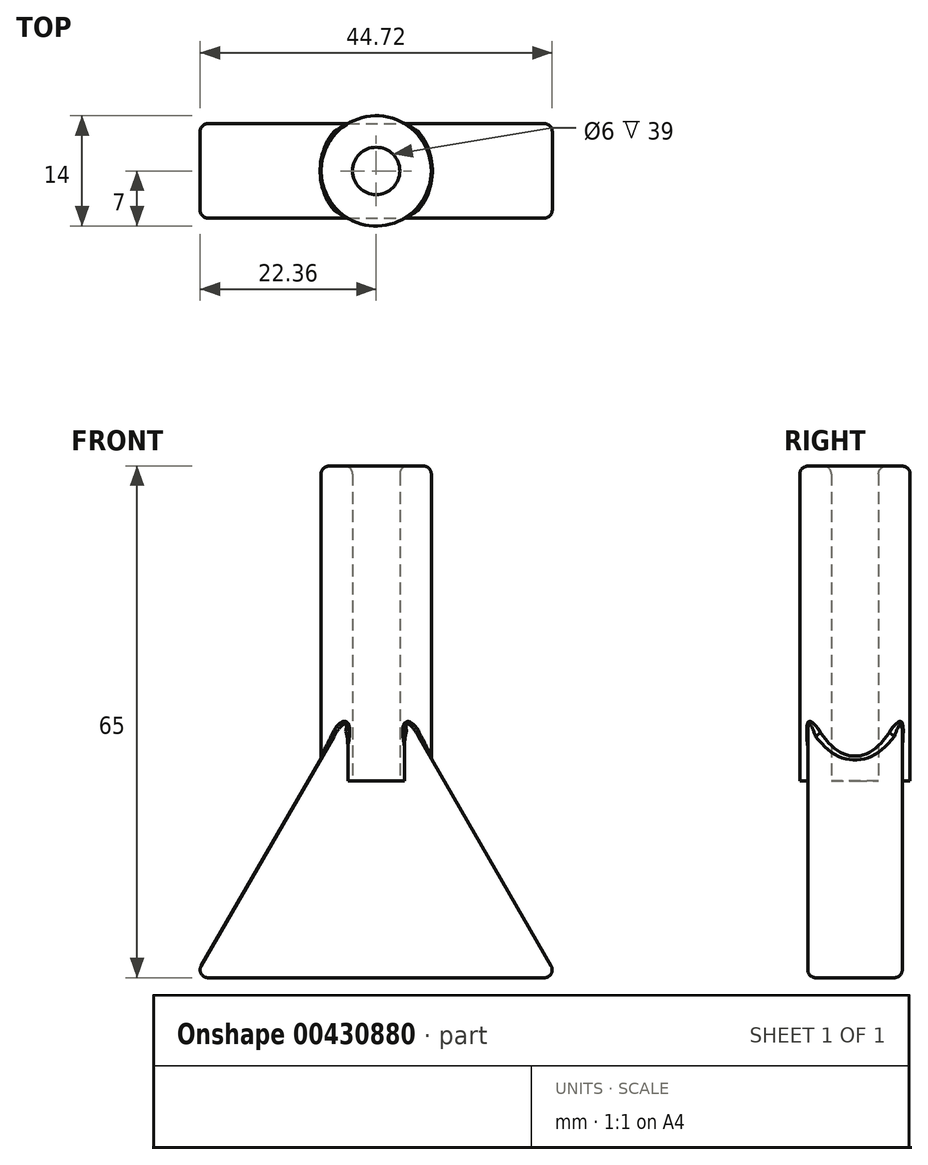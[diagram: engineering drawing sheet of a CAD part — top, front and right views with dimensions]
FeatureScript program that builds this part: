
annotation { "Feature Type Name" : "Feature", "Feature Type Description" : "" }
export const myFeature = defineFeature(function(context is Context, id is Id, definition is map)
    precondition{}
    {
        {
            var Q0;
            Q0=qCreatedBy(makeId("Top.planeOp"),FACE);
            var sketch = newSketch(context, id + "F0", { "sketchPlane" : qUnion([Q0])});
            skCircle(sketch, "E0", {"center": v(0, 0) * mm, "radius": 3 * mm});
            skCircle(sketch, "E1", {"center": v(0, 0) * mm, "radius": 7 * mm});
            skSolve(sketch);
        }
        {
            var Q0;
            Q0=makeQuery(id+"F0.imprint","IMPRINT",FACE,{"disambiguationData":[TD([[makeQuery(id+"F0.imprint","IMPRINT",EDGE,{"derivedFrom":sQuery(id+"F0.wireOp",EDGE,"E0")}),-1.0]])]});
            extrude(context, id + "F1", {"entities" : qUnion([Q0]), "depth" : 40 * mm});
        }
        {
            var Q0;
            Q0=qCreatedBy(makeId("Front.planeOp"),FACE);
            var sketch = newSketch(context, id + "F2", { "sketchPlane" : qUnion([Q0])});
            skLineSegment(sketch, "E2", {"start": v(0, 15) * mm, "end": v(-23.1, -25) * mm});
            skLineSegment(sketch, "E3", {"start": v(-23.1, -25) * mm, "end": v(23.1, -25) * mm});
            skLineSegment(sketch, "E4", {"start": v(23.1, -25) * mm, "end": v(0, 15) * mm});
            skSolve(sketch);
        }
        {
            var Q0;
            Q0=makeQuery(id+"F2.imprint","IMPRINT",FACE,{"disambiguationData":[TD([[makeQuery(id+"F2.imprint","IMPRINT",EDGE,{"derivedFrom":sQuery(id+"F2.wireOp",EDGE,"E2")}),1.0]])]});
            extrude(context, id + "F3", {"entities" : qUnion([Q0]), "operationType" : NewBodyOperationType.ADD, "endBound" : BoundingType.SYMMETRIC, "depth" : 12 * mm});
        }
        {
            var Q0;
            Q0=makeQuery(id+"F3.opExtrude","CAP_EDGE",EDGE,{"disambiguationData":[OSD([sQuery(id+"F2.wireOp",EDGE,"E2")])],"isStart":false});
            var Q1;
            Q1=makeQuery(id+"F3.opExtrude","CAP_EDGE",EDGE,{"disambiguationData":[OSD([sQuery(id+"F2.wireOp",EDGE,"E2")])],"isStart":true});
            var Q2;
            Q2=makeQuery(id+"F3.opExtrude","CAP_EDGE",EDGE,{"disambiguationData":[OSD([sQuery(id+"F2.wireOp",EDGE,"E4")])],"isStart":false});
            var Q3;
            Q3=makeQuery(id+"F3.opExtrude","CAP_EDGE",EDGE,{"disambiguationData":[OSD([sQuery(id+"F2.wireOp",EDGE,"E4")])],"isStart":true});
            var Q4;
            Q4=makeQuery(id+"F3.boolean.opBoolean","INTERSECT",EDGE,{"derivedFrom":[makeQuery(id+"F1.opExtrude","SWEPT_FACE",FACE,{"disambiguationData":[OSD([sQuery(id+"F0.wireOp",EDGE,"E1")])]}),makeQuery(id+"F3.opExtrude","SWEPT_FACE",FACE,{"disambiguationData":[OSD([sQuery(id+"F2.wireOp",EDGE,"E4")])]})]});
            var Q5;
            Q5=makeQuery(id+"F3.boolean.opBoolean","INTERSECT",EDGE,{"derivedFrom":[makeQuery(id+"F1.opExtrude","SWEPT_FACE",FACE,{"disambiguationData":[OSD([sQuery(id+"F0.wireOp",EDGE,"E1")])]}),makeQuery(id+"F3.opExtrude","SWEPT_FACE",FACE,{"disambiguationData":[OSD([sQuery(id+"F2.wireOp",EDGE,"E2")])]})]});
            var Q6;
            Q6=makeQuery(id+"F3.opExtrude","SWEPT_EDGE",EDGE,{"disambiguationData":[OSD([sQuery(id+"F2.wireOp",EDGE,"E2"),sQuery(id+"F2.wireOp",EDGE,"E3")])]});
            var Q7;
            Q7=makeQuery(id+"F3.opExtrude","CAP_EDGE",EDGE,{"disambiguationData":[OSD([sQuery(id+"F2.wireOp",EDGE,"E3")])],"isStart":false});
            var Q8;
            Q8=makeQuery(id+"F3.opExtrude","CAP_EDGE",EDGE,{"disambiguationData":[OSD([sQuery(id+"F2.wireOp",EDGE,"E3")])],"isStart":true});
            var Q9;
            Q9=makeQuery(id+"F3.opExtrude","SWEPT_EDGE",EDGE,{"disambiguationData":[OSD([sQuery(id+"F2.wireOp",EDGE,"E3"),sQuery(id+"F2.wireOp",EDGE,"E4")])]});
            fillet(context, id + "F4", {"entities" : qUnion([Q0, Q1, Q2, Q3, Q4, Q5, Q6, Q7, Q8, Q9]), "radius" : 1 * mm, "tangentPropagation" : true, "allowEdgeOverflow" : false});
        }
        {
            var Q0;
            Q0=makeQuery(id+"F1.opExtrude","CAP_EDGE",EDGE,{"disambiguationData":[OSD([sQuery(id+"F0.wireOp",EDGE,"E0")])],"isStart":false});
            var Q1;
            Q1=makeQuery(id+"F1.opExtrude","CAP_EDGE",EDGE,{"disambiguationData":[OSD([sQuery(id+"F0.wireOp",EDGE,"E1")])],"isStart":false});
            fillet(context, id + "F5", {"entities" : qUnion([Q0, Q1]), "radius" : 1 * mm, "tangentPropagation" : true, "allowEdgeOverflow" : false});
        }
        {
            var Q0;
            Q0=qCreatedBy(makeId("Top.planeOp"),FACE);
            var sketch = newSketch(context, id + "F6", { "sketchPlane" : qUnion([Q0])});
            skCircle(sketch, "E5", {"center": v(0, 0) * mm, "radius": 3 * mm});
            skSolve(sketch);
        }
        {
            var Q0;
            Q0 = qSketchRegion(id + "F6", true);
            extrude(context, id + "F7", {"entities" : qUnion([Q0]), "operationType" : NewBodyOperationType.REMOVE, "depth" : 25 * mm});
        }
    });
